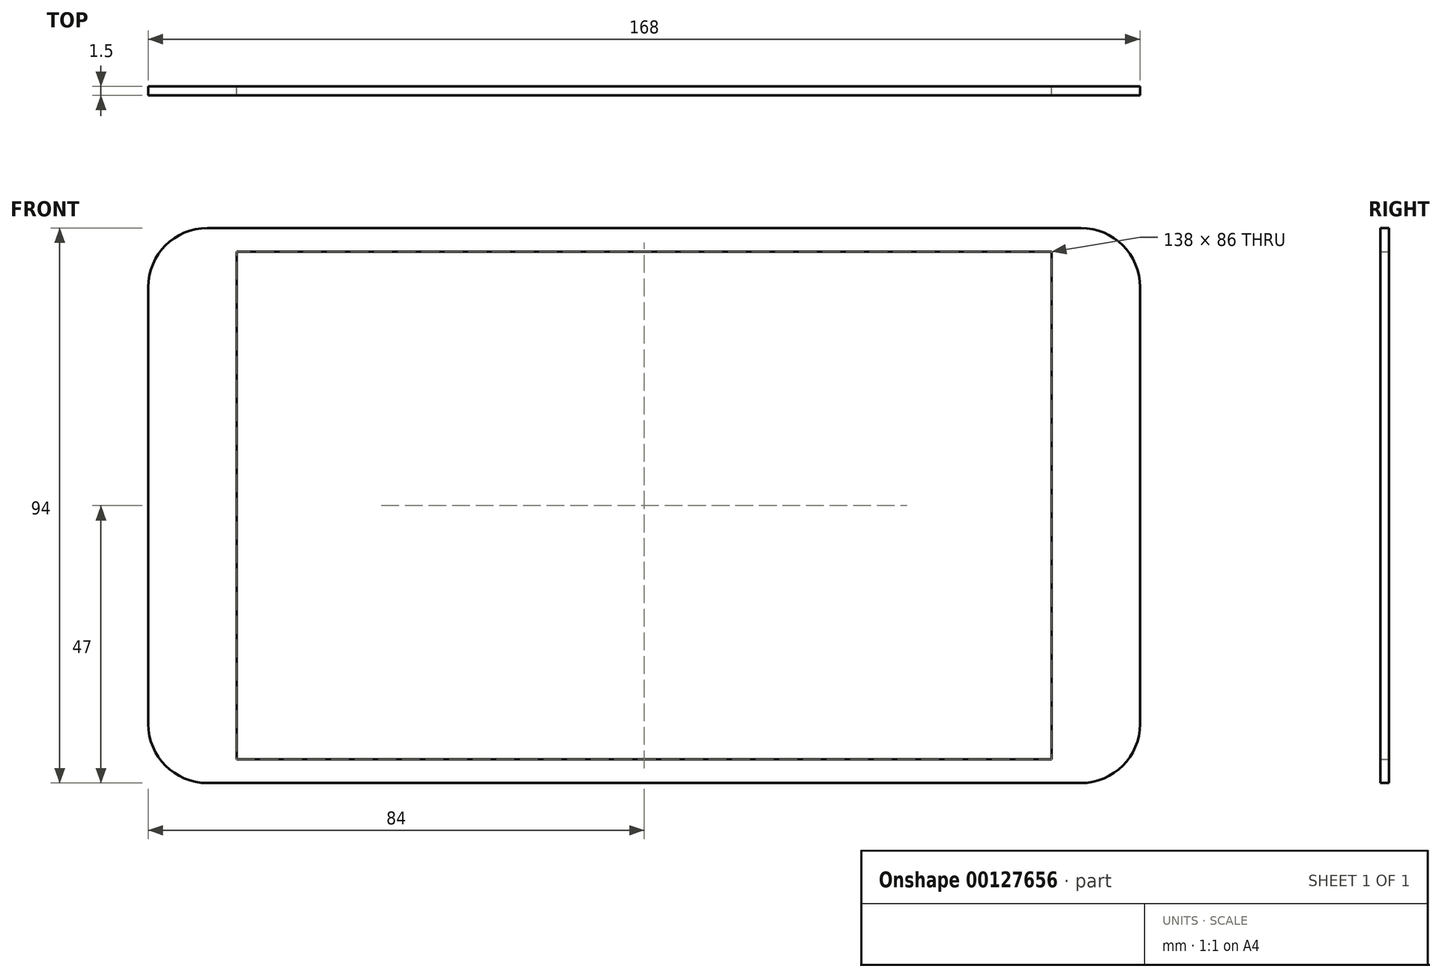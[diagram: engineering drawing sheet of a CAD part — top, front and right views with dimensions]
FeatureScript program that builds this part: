
annotation { "Feature Type Name" : "Feature", "Feature Type Description" : "" }
export const myFeature = defineFeature(function(context is Context, id is Id, definition is map)
    precondition{}
    {
        {
            var Q0;
            Q0=qCreatedBy(makeId("Front.planeOp"),FACE);
            var sketch = newSketch(context, id + "F0", { "sketchPlane" : qUnion([Q0])});
            skLineSegment(sketch, "E0.bottom", {"start": v(74, 47) * mm, "end": v(-74, 47) * mm});
            skLineSegment(sketch, "E0.top", {"start": v(74, -47) * mm, "end": v(-74, -47) * mm});
            skLineSegment(sketch, "E0.left", {"start": v(84, 37) * mm, "end": v(84, -37) * mm});
            skLineSegment(sketch, "E0.right", {"start": v(-84, 37) * mm, "end": v(-84, -37) * mm});
            skPoint(sketch, "E0.middle", {"position": v(0, 0) * mm});
            skPoint(sketch, "E1.visualSharp", {"position": v(-84, 47) * mm});
            skArc(sketch, "E1.filletArc", {"start": v(-74, 47) * mm, "mid": v(-81.07, 44.07) * mm, "end": v(-84, 37) * mm});
            skPoint(sketch, "E2.visualSharp", {"position": v(-84, -47) * mm});
            skArc(sketch, "E2.filletArc", {"start": v(-84, -37) * mm, "mid": v(-81.07, -44.07) * mm, "end": v(-74, -47) * mm});
            skPoint(sketch, "E3.visualSharp", {"position": v(84, -47) * mm});
            skArc(sketch, "E3.filletArc", {"start": v(74, -47) * mm, "mid": v(81.07, -44.07) * mm, "end": v(84, -37) * mm});
            skPoint(sketch, "E4.visualSharp", {"position": v(84, 47) * mm});
            skArc(sketch, "E4.filletArc", {"start": v(84, 37) * mm, "mid": v(81.07, 44.07) * mm, "end": v(74, 47) * mm});
            skLineSegment(sketch, "E5.bottom", {"start": v(69, 43) * mm, "end": v(-69, 43) * mm});
            skLineSegment(sketch, "E5.top", {"start": v(69, -43) * mm, "end": v(-69, -43) * mm});
            skLineSegment(sketch, "E5.left", {"start": v(69, 43) * mm, "end": v(69, -43) * mm});
            skLineSegment(sketch, "E5.right", {"start": v(-69, 43) * mm, "end": v(-69, -43) * mm});
            skSolve(sketch);
        }
        {
            var Q0;
            Q0 = qSketchRegion(id + "F0", true);
            extrude(context, id + "F1", {"entities" : qUnion([Q0]), "depth" : 1.5 * mm});
        }
    });
